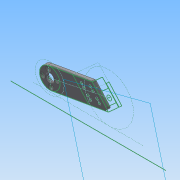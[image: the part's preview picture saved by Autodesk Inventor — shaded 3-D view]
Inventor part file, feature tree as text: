
AUTODESK INVENTOR PART (.ipt)
format: ipt  version: 2014 SP2 (Build 180246200, 246)  size: 224,768 bytes
history: native  units: in
note: dims shown in document units (in); Inventor stores cm internally (conversion verified against a paired STEP export)
features: other x2, extrude x2, hole x2, fillet x1, pattern_linear x1, sketch x1
ambient origin geometry x8: Origin, YZ Plane, XZ Plane, XY Plane, X Axis, Y Axis, Z Axis, Center Point
bodies: Solid1 (feature_tree)
feature tree (9):
  other  "MountSketch.ipt"
  extrude  "Extrusion1"  Depth=0.25in TaperAngle=0.0deg
  hole  "Hole2"  [1 undecoded]
  hole  "Hole3"  [1 undecoded]
  extrude  "Attachment Holes"  Depth=0.25in
  fillet  "Fillet1"  [1 undecoded]
  pattern_linear  "Extra Holes"  [2 undecoded]
  other  "Axle Centers"
  sketch  "Sketch2"  dims[d0=0.3937in d1=0.25in d2=0.0in d10=0.6in d11=0.75in d12=0.375in d13=0.25in d14=0.5635in d15=1.0in d16=0.8108in d17=0.177in d18=0.75in d19=0.37in d20=0.25in d21=90.0deg d22=1.0in d23=0.8108in d24=1.0in d25=0.0in d26=0.125in d27=0.7874in d29=0.25in]
note: 5 required parameter values undecoded (feature->parameter linkage not recoverable at this tier; creation-order binding heuristic only, values carry confidence <= 0.55)
